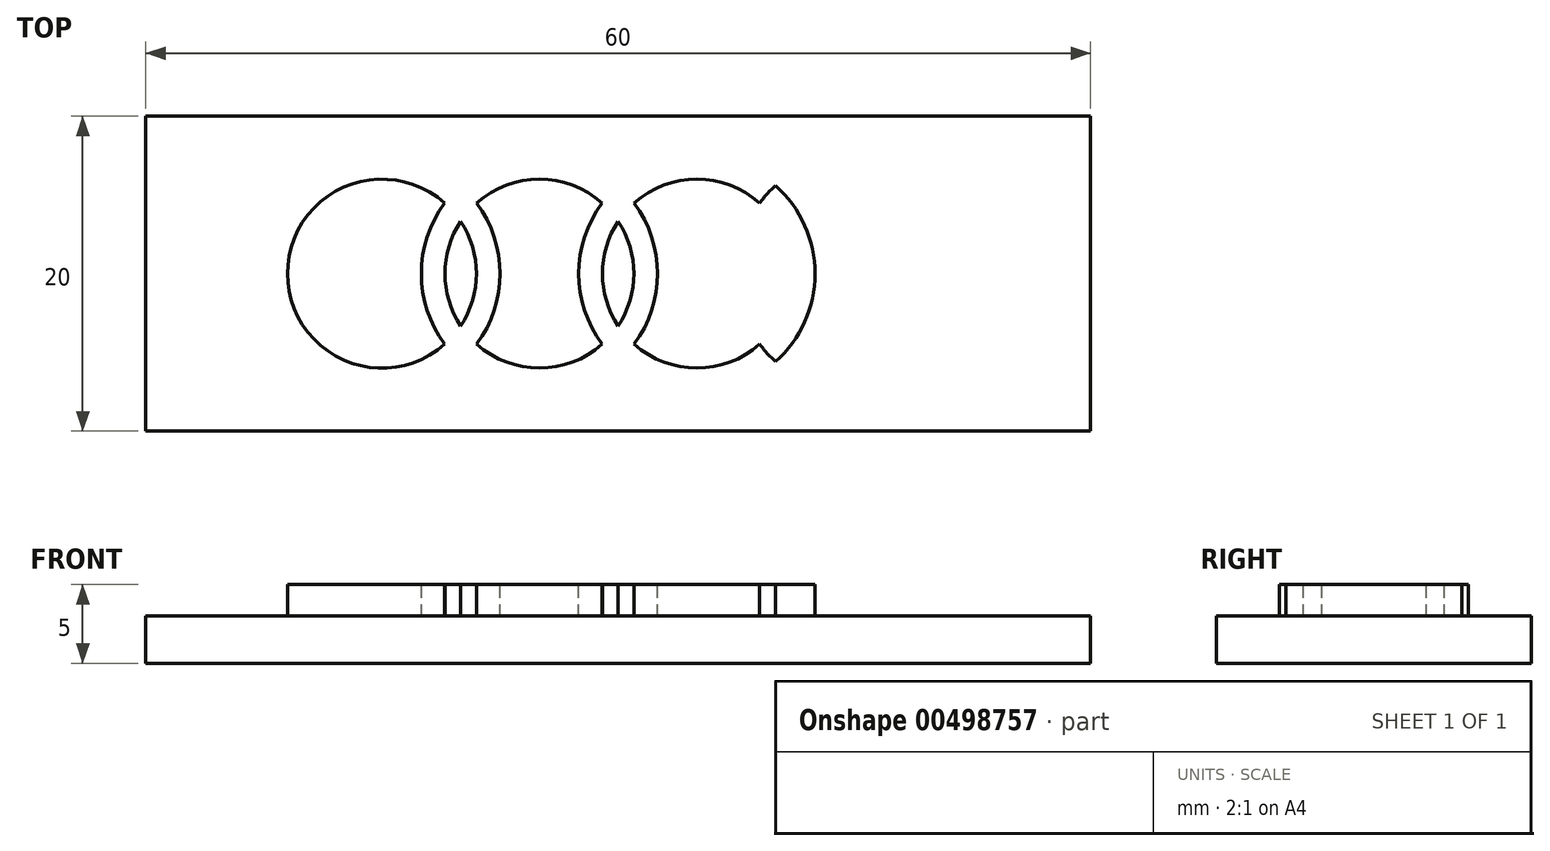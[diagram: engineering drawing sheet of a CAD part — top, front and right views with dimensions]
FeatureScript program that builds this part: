
annotation { "Feature Type Name" : "Feature", "Feature Type Description" : "" }
export const myFeature = defineFeature(function(context is Context, id is Id, definition is map)
    precondition{}
    {
        {
            var Q0;
            Q0=qCreatedBy(makeId("Top.planeOp"),FACE);
            var sketch = newSketch(context, id + "F0", { "sketchPlane" : qUnion([Q0])});
            skLineSegment(sketch, "E0.bottom", {"start": v(30, -10) * mm, "end": v(-30, -10) * mm});
            skLineSegment(sketch, "E0.top", {"start": v(30, 10) * mm, "end": v(-30, 10) * mm});
            skLineSegment(sketch, "E0.left", {"start": v(30, -10) * mm, "end": v(30, 10) * mm});
            skLineSegment(sketch, "E0.right", {"start": v(-30, -10) * mm, "end": v(-30, 10) * mm});
            skPoint(sketch, "E0.middle", {"position": v(0, 0) * mm});
            skSolve(sketch);
        }
        {
            var Q0;
            Q0=makeQuery(id+"F0.imprint","IMPRINT",FACE,{"disambiguationData":[TD([[makeQuery(id+"F0.imprint","IMPRINT",EDGE,{"derivedFrom":sQuery(id+"F0.wireOp",EDGE,"E0.bottom")}),-1.0]])]});
            extrude(context, id + "F1", {"entities" : qUnion([Q0]), "depth" : 5 * mm});
        }
        {
            var Q0;
            Q0=makeQuery(id+"F1.opExtrude","CAP_FACE",FACE,{"disambiguationData":[OSD([sQuery(id+"F0.wireOp",EDGE,"E0.bottom"),sQuery(id+"F0.wireOp",EDGE,"E0.top"),sQuery(id+"F0.wireOp",EDGE,"E0.left"),sQuery(id+"F0.wireOp",EDGE,"E0.right")])],"isStart":false});
            var sketch = newSketch(context, id + "F2", { "sketchPlane" : qUnion([Q0])});
            skCircle(sketch, "E1", {"center": v(-15, 0) * mm, "radius": 7.5 * mm});
            skCircle(sketch, "E2", {"center": v(-15, 0) * mm, "radius": 6 * mm});
            skCircle(sketch, "E3", {"center": v(-5, 0) * mm, "radius": 6 * mm});
            skCircle(sketch, "E4", {"center": v(-5, 0) * mm, "radius": 7.5 * mm});
            skCircle(sketch, "E5.MirrorC", {"center": v(5, 0) * mm, "radius": 7.5 * mm});
            skCircle(sketch, "E6.MirrorC", {"center": v(5, 0) * mm, "radius": 6 * mm});
            skCircle(sketch, "E7.MirrorC", {"center": v(15, 0) * mm, "radius": 7.5 * mm});
            skCircle(sketch, "E8.MirrorC", {"center": v(15, 0) * mm, "radius": 6 * mm});
            skSolve(sketch);
        }
        {
            var Q0;
            {var subQ0=sQuery(id+"F2.wireOp",EDGE,"E4");var subQ1=sQuery(id+"F2.wireOp",EDGE,"E1");var subQ2=makeQuery(id+"F2.imprint","INTERSECT",VERTEX,{"disambiguationData":[OD(0.0)],"derivedFrom":[subQ1,subQ0]});Q0=makeQuery(id+"F2.imprint","IMPRINT",FACE,{"disambiguationData":[TD([[makeQuery(id+"F2.imprint","IMPRINT",EDGE,{"disambiguationData":[TD([[subQ2,-1.0]])],"derivedFrom":subQ1}),1.0]])]});}
            var Q1;
            {var subQ0=sQuery(id+"F2.wireOp",EDGE,"E4");var subQ1=sQuery(id+"F2.wireOp",EDGE,"E2");var subQ2=makeQuery(id+"F2.imprint","INTERSECT",VERTEX,{"disambiguationData":[OD(0.0)],"derivedFrom":[subQ1,subQ0]});Q1=makeQuery(id+"F2.imprint","IMPRINT",FACE,{"disambiguationData":[TD([[makeQuery(id+"F2.imprint","IMPRINT",EDGE,{"disambiguationData":[TD([[subQ2,1.0]])],"derivedFrom":subQ1}),1.0]])]});}
            var Q2;
            {var subQ0=sQuery(id+"F2.wireOp",EDGE,"E4");var subQ1=sQuery(id+"F2.wireOp",EDGE,"E1");var subQ2=makeQuery(id+"F2.imprint","INTERSECT",VERTEX,{"disambiguationData":[OD(0.0)],"derivedFrom":[subQ1,subQ0]});Q2=makeQuery(id+"F2.imprint","IMPRINT",FACE,{"disambiguationData":[TD([[makeQuery(id+"F2.imprint","IMPRINT",EDGE,{"disambiguationData":[TD([[subQ2,1.0]])],"derivedFrom":subQ1}),-1.0]])]});}
            var Q3;
            {var subQ0=sQuery(id+"F2.wireOp",EDGE,"E4");var subQ1=sQuery(id+"F2.wireOp",EDGE,"E1");var subQ2=makeQuery(id+"F2.imprint","INTERSECT",VERTEX,{"disambiguationData":[OD(1.0)],"derivedFrom":[subQ1,subQ0]});Q3=makeQuery(id+"F2.imprint","IMPRINT",FACE,{"disambiguationData":[TD([[makeQuery(id+"F2.imprint","IMPRINT",EDGE,{"disambiguationData":[TD([[subQ2,-1.0]])],"derivedFrom":subQ1}),-1.0]])]});}
            var Q4;
            {var subQ0=sQuery(id+"F2.wireOp",EDGE,"E6.MirrorC");var subQ1=sQuery(id+"F2.wireOp",EDGE,"E3");var subQ2=makeQuery(id+"F2.imprint","INTERSECT",VERTEX,{"disambiguationData":[OD(0.0)],"derivedFrom":[subQ1,subQ0]});Q4=makeQuery(id+"F2.imprint","IMPRINT",FACE,{"disambiguationData":[TD([[makeQuery(id+"F2.imprint","IMPRINT",EDGE,{"disambiguationData":[TD([[subQ2,1.0]])],"derivedFrom":subQ1}),-1.0]])]});}
            var Q5;
            {var subQ0=sQuery(id+"F2.wireOp",EDGE,"E3");var subQ1=sQuery(id+"F2.wireOp",EDGE,"E1");var subQ2=makeQuery(id+"F2.imprint","INTERSECT",VERTEX,{"disambiguationData":[OD(0.0)],"derivedFrom":[subQ1,subQ0]});Q5=makeQuery(id+"F2.imprint","IMPRINT",FACE,{"disambiguationData":[TD([[makeQuery(id+"F2.imprint","IMPRINT",EDGE,{"disambiguationData":[TD([[subQ2,1.0]])],"derivedFrom":subQ1}),1.0]])]});}
            var Q6;
            {var subQ0=sQuery(id+"F2.wireOp",EDGE,"E4");var subQ1=sQuery(id+"F2.wireOp",EDGE,"E1");var subQ2=makeQuery(id+"F2.imprint","INTERSECT",VERTEX,{"disambiguationData":[OD(0.0)],"derivedFrom":[subQ1,subQ0]});Q6=makeQuery(id+"F2.imprint","IMPRINT",FACE,{"disambiguationData":[TD([[makeQuery(id+"F2.imprint","IMPRINT",EDGE,{"disambiguationData":[TD([[subQ2,1.0]])],"derivedFrom":subQ1}),1.0]])]});}
            var Q7;
            {var subQ0=sQuery(id+"F2.wireOp",EDGE,"E4");var subQ1=sQuery(id+"F2.wireOp",EDGE,"E1");var subQ2=makeQuery(id+"F2.imprint","INTERSECT",VERTEX,{"disambiguationData":[OD(1.0)],"derivedFrom":[subQ1,subQ0]});Q7=makeQuery(id+"F2.imprint","IMPRINT",FACE,{"disambiguationData":[TD([[makeQuery(id+"F2.imprint","IMPRINT",EDGE,{"disambiguationData":[TD([[subQ2,-1.0]])],"derivedFrom":subQ1}),1.0]])]});}
            var Q8;
            {var subQ0=sQuery(id+"F2.wireOp",EDGE,"E5.MirrorC");var subQ1=sQuery(id+"F2.wireOp",EDGE,"E3");var subQ2=makeQuery(id+"F2.imprint","INTERSECT",VERTEX,{"disambiguationData":[OD(0.0)],"derivedFrom":[subQ1,subQ0]});Q8=makeQuery(id+"F2.imprint","IMPRINT",FACE,{"disambiguationData":[TD([[makeQuery(id+"F2.imprint","IMPRINT",EDGE,{"disambiguationData":[TD([[subQ2,1.0]])],"derivedFrom":subQ1}),-1.0]])]});}
            var Q9;
            {var subQ0=sQuery(id+"F2.wireOp",EDGE,"E5.MirrorC");var subQ1=sQuery(id+"F2.wireOp",EDGE,"E3");var subQ2=makeQuery(id+"F2.imprint","INTERSECT",VERTEX,{"disambiguationData":[OD(1.0)],"derivedFrom":[subQ1,subQ0]});Q9=makeQuery(id+"F2.imprint","IMPRINT",FACE,{"disambiguationData":[TD([[makeQuery(id+"F2.imprint","IMPRINT",EDGE,{"disambiguationData":[TD([[subQ2,-1.0]])],"derivedFrom":subQ1}),-1.0]])]});}
            var Q10;
            {var subQ0=sQuery(id+"F2.wireOp",EDGE,"E5.MirrorC");var subQ1=sQuery(id+"F2.wireOp",EDGE,"E3");var subQ2=makeQuery(id+"F2.imprint","INTERSECT",VERTEX,{"disambiguationData":[OD(0.0)],"derivedFrom":[subQ1,subQ0]});Q10=makeQuery(id+"F2.imprint","IMPRINT",FACE,{"disambiguationData":[TD([[makeQuery(id+"F2.imprint","IMPRINT",EDGE,{"disambiguationData":[TD([[subQ2,1.0]])],"derivedFrom":subQ1}),1.0]])]});}
            var Q11;
            {var subQ0=sQuery(id+"F2.wireOp",EDGE,"E5.MirrorC");var subQ1=sQuery(id+"F2.wireOp",EDGE,"E4");var subQ2=makeQuery(id+"F2.imprint","INTERSECT",VERTEX,{"disambiguationData":[OD(0.0)],"derivedFrom":[subQ1,subQ0]});Q11=makeQuery(id+"F2.imprint","IMPRINT",FACE,{"disambiguationData":[TD([[makeQuery(id+"F2.imprint","IMPRINT",EDGE,{"disambiguationData":[TD([[subQ2,1.0]])],"derivedFrom":subQ1}),-1.0]])]});}
            var Q12;
            {var subQ0=sQuery(id+"F2.wireOp",EDGE,"E5.MirrorC");var subQ1=sQuery(id+"F2.wireOp",EDGE,"E4");var subQ2=makeQuery(id+"F2.imprint","INTERSECT",VERTEX,{"disambiguationData":[OD(1.0)],"derivedFrom":[subQ1,subQ0]});Q12=makeQuery(id+"F2.imprint","IMPRINT",FACE,{"disambiguationData":[TD([[makeQuery(id+"F2.imprint","IMPRINT",EDGE,{"disambiguationData":[TD([[subQ2,-1.0]])],"derivedFrom":subQ1}),-1.0]])]});}
            var Q13;
            {var subQ0=sQuery(id+"F2.wireOp",EDGE,"E8.MirrorC");var subQ1=sQuery(id+"F2.wireOp",EDGE,"E5.MirrorC");var subQ2=makeQuery(id+"F2.imprint","INTERSECT",VERTEX,{"disambiguationData":[OD(1.0)],"derivedFrom":[subQ1,subQ0]});Q13=makeQuery(id+"F2.imprint","IMPRINT",FACE,{"disambiguationData":[TD([[makeQuery(id+"F2.imprint","IMPRINT",EDGE,{"disambiguationData":[TD([[subQ2,-1.0]])],"derivedFrom":subQ1}),-1.0]])]});}
            var Q14;
            {var subQ0=sQuery(id+"F2.wireOp",EDGE,"E8.MirrorC");var subQ1=sQuery(id+"F2.wireOp",EDGE,"E5.MirrorC");var subQ2=makeQuery(id+"F2.imprint","INTERSECT",VERTEX,{"disambiguationData":[OD(0.0)],"derivedFrom":[subQ1,subQ0]});Q14=makeQuery(id+"F2.imprint","IMPRINT",FACE,{"disambiguationData":[TD([[makeQuery(id+"F2.imprint","IMPRINT",EDGE,{"disambiguationData":[TD([[subQ2,-1.0]])],"derivedFrom":subQ1}),-1.0]])]});}
            var Q15;
            {var subQ0=sQuery(id+"F2.wireOp",EDGE,"E7.MirrorC");var subQ1=sQuery(id+"F2.wireOp",EDGE,"E6.MirrorC");var subQ2=makeQuery(id+"F2.imprint","INTERSECT",VERTEX,{"disambiguationData":[OD(0.0)],"derivedFrom":[subQ1,subQ0]});Q15=makeQuery(id+"F2.imprint","IMPRINT",FACE,{"disambiguationData":[TD([[makeQuery(id+"F2.imprint","IMPRINT",EDGE,{"disambiguationData":[TD([[subQ2,-1.0]])],"derivedFrom":subQ1}),-1.0]])]});}
            var Q16;
            {var subQ0=sQuery(id+"F2.wireOp",EDGE,"E7.MirrorC");var subQ1=sQuery(id+"F2.wireOp",EDGE,"E5.MirrorC");var subQ2=makeQuery(id+"F2.imprint","INTERSECT",VERTEX,{"disambiguationData":[OD(0.0)],"derivedFrom":[subQ1,subQ0]});Q16=makeQuery(id+"F2.imprint","IMPRINT",FACE,{"disambiguationData":[TD([[makeQuery(id+"F2.imprint","IMPRINT",EDGE,{"disambiguationData":[TD([[subQ2,-1.0]])],"derivedFrom":subQ1}),-1.0]])]});}
            var Q17;
            {var subQ0=sQuery(id+"F2.wireOp",EDGE,"E7.MirrorC");var subQ1=sQuery(id+"F2.wireOp",EDGE,"E5.MirrorC");var subQ2=makeQuery(id+"F2.imprint","INTERSECT",VERTEX,{"disambiguationData":[OD(0.0)],"derivedFrom":[subQ1,subQ0]});Q17=makeQuery(id+"F2.imprint","IMPRINT",FACE,{"disambiguationData":[TD([[makeQuery(id+"F2.imprint","IMPRINT",EDGE,{"disambiguationData":[TD([[subQ2,-1.0]])],"derivedFrom":subQ1}),1.0]])]});}
            extrude(context, id + "F3", {"entities" : qUnion([Q0, Q1, Q2, Q3, Q4, Q5, Q6, Q7, Q8, Q9, Q10, Q11, Q12, Q13, Q14, Q15, Q16, Q17]), "operationType" : NewBodyOperationType.REMOVE, "oppositeDirection" : true, "depth" : 2 * mm});
        }
    });
